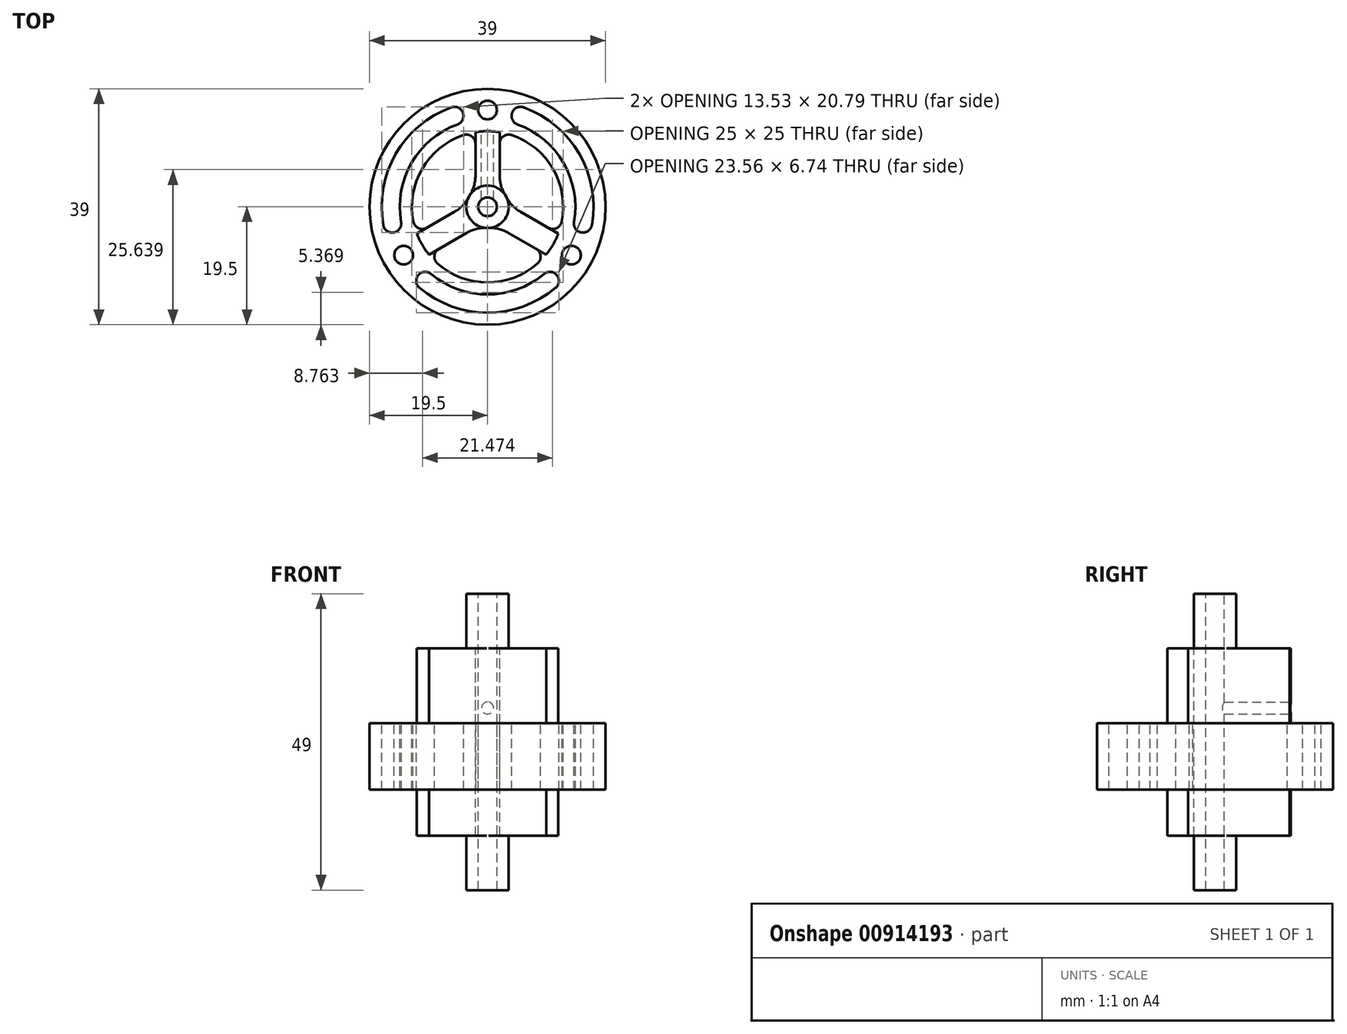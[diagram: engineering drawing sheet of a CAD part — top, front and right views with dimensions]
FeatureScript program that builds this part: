
annotation { "Feature Type Name" : "Feature", "Feature Type Description" : "" }
export const myFeature = defineFeature(function(context is Context, id is Id, definition is map)
    precondition{}
    {
        {
            var Q0;
            Q0=qCreatedBy(makeId("Front.planeOp"),FACE);
            var sketch = newSketch(context, id + "F0", { "sketchPlane" : qUnion([Q0])});
            skLineSegment(sketch, "E0", {"start": v(1.55, 49) * mm, "end": v(3.5, 49) * mm});
            skLineSegment(sketch, "E1", {"start": v(3.5, 49) * mm, "end": v(3.5, 40) * mm});
            skLineSegment(sketch, "E2", {"start": v(3.5, 40) * mm, "end": v(12.5, 40) * mm});
            skLineSegment(sketch, "E3", {"start": v(12.5, 40) * mm, "end": v(12.5, 27.6) * mm});
            skLineSegment(sketch, "E4", {"start": v(12.5, 27.6) * mm, "end": v(19.5, 27.6) * mm});
            skLineSegment(sketch, "E5", {"start": v(19.5, 27.6) * mm, "end": v(19.5, 16.6) * mm});
            skLineSegment(sketch, "E6", {"start": v(19.5, 16.6) * mm, "end": v(12.5, 16.6) * mm});
            skLineSegment(sketch, "E7", {"start": v(12.5, 16.6) * mm, "end": v(12.5, 9) * mm});
            skLineSegment(sketch, "E8", {"start": v(12.5, 9) * mm, "end": v(3.5, 9) * mm});
            skLineSegment(sketch, "E9", {"start": v(3.5, 9) * mm, "end": v(3.5, 0) * mm});
            skLineSegment(sketch, "E10", {"start": v(3.5, 0) * mm, "end": v(1.55, 0) * mm});
            skLineSegment(sketch, "E11", {"start": v(1.55, 49) * mm, "end": v(1.55, 0) * mm});
            skLineSegment(sketch, "E12", {"start": v(0, 52.95) * mm, "end": v(0, -2.67) * mm, "construction": true});
            skSolve(sketch);
        }
        {
            var Q0;
            Q0=makeQuery(id+"F0.imprint","IMPRINT",FACE,{"disambiguationData":[TD([[makeQuery(id+"F0.imprint","IMPRINT",EDGE,{"derivedFrom":sQuery(id+"F0.wireOp",EDGE,"E0")}),-1.0]])]});
            var Q1;
            Q1=sQuery(id+"F0.wireOp",EDGE,"E12");
            revolve(context, id + "F1", {"surfaceOperationType" : NewSurfaceOperationType.NEW, "entities" : qUnion([Q0]), "axis" : qUnion([Q1]), "revolveType" : RevolveType.FULL});
        }
        {
            var Q0;
            Q0=makeQuery(id+"F1.opRevolve","SWEPT_FACE",FACE,{"disambiguationData":[OSD([sQuery(id+"F0.wireOp",EDGE,"E4")])]});
            var sketch = newSketch(context, id + "F2", { "sketchPlane" : qUnion([Q0])});
            skCircle(sketch, "E13", {"center": v(0, 16) * mm, "radius": 1.55 * mm});
            skCircle(sketch, "E14.1.0", {"center": v(-13.86, -8) * mm, "radius": 1.55 * mm});
            skCircle(sketch, "E14.2.0", {"center": v(13.86, -8) * mm, "radius": 1.55 * mm});
            skPoint(sketch, "E14.center", {"position": v(0, 0) * mm});
            skArc(sketch, "E15", {"start": v(5.99, 16.44) * mm, "mid": v(15.16, 8.75) * mm, "end": v(17.23, -3.04) * mm});
            skArc(sketch, "E16", {"start": v(4.96, 13.63) * mm, "mid": v(12.56, 7.25) * mm, "end": v(14.28, -2.52) * mm});
            skArc(sketch, "E17", {"start": v(14.28, -2.52) * mm, "mid": v(15.5, -4.26) * mm, "end": v(17.23, -3.04) * mm});
            skArc(sketch, "E18", {"start": v(4.96, 13.63) * mm, "mid": v(4.06, 15.55) * mm, "end": v(5.99, 16.44) * mm});
            skLineSegment(sketch, "E19", {"start": v(0, 0) * mm, "end": v(5.47, 15.04) * mm, "construction": true});
            skLineSegment(sketch, "E20", {"start": v(0, 0) * mm, "end": v(15.76, -2.78) * mm, "construction": true});
            skArc(sketch, "E21.1.0", {"start": v(-14.28, -2.52) * mm, "mid": v(-12.56, 7.25) * mm, "end": v(-4.96, 13.63) * mm});
            skArc(sketch, "E21.1.1", {"start": v(-14.28, -2.52) * mm, "mid": v(-15.5, -4.26) * mm, "end": v(-17.23, -3.04) * mm});
            skArc(sketch, "E21.1.2", {"start": v(-17.23, -3.04) * mm, "mid": v(-15.16, 8.75) * mm, "end": v(-5.99, 16.44) * mm});
            skArc(sketch, "E21.1.3", {"start": v(-4.96, 13.63) * mm, "mid": v(-4.06, 15.55) * mm, "end": v(-5.99, 16.44) * mm});
            skArc(sketch, "E21.2.0", {"start": v(9.32, -11.1) * mm, "mid": v(0, -14.5) * mm, "end": v(-9.32, -11.1) * mm});
            skArc(sketch, "E21.2.1", {"start": v(9.32, -11.1) * mm, "mid": v(11.43, -11.3) * mm, "end": v(11.25, -13.4) * mm});
            skArc(sketch, "E21.2.2", {"start": v(11.25, -13.4) * mm, "mid": v(0, -17.5) * mm, "end": v(-11.25, -13.4) * mm});
            skArc(sketch, "E21.2.3", {"start": v(-9.32, -11.1) * mm, "mid": v(-11.43, -11.3) * mm, "end": v(-11.25, -13.4) * mm});
            skSolve(sketch);
        }
        {
            var Q0;
            Q0 = qSketchRegion(id + "F2", true);
            extrude(context, id + "F3", {"entities" : qUnion([Q0]), "operationType" : NewBodyOperationType.REMOVE, "endBound" : BoundingType.THROUGH_ALL, "oppositeDirection" : true, "depth" : 25 * mm, "offsetDistance" : 25 * mm});
        }
        {
            var Q0;
            Q0=makeQuery(id+"F1.opRevolve","SWEPT_FACE",FACE,{"disambiguationData":[OSD([sQuery(id+"F0.wireOp",EDGE,"E2")])]});
            var sketch = newSketch(context, id + "F4", { "sketchPlane" : qUnion([Q0])});
            skLineSegment(sketch, "E22", {"start": v(2, 5.12) * mm, "end": v(2, 12.34) * mm});
            skLineSegment(sketch, "E23", {"start": v(0, 0) * mm, "end": v(18.8, -10.86) * mm, "construction": true});
            skLineSegment(sketch, "E24", {"start": v(5.44, -0.83) * mm, "end": v(11.69, -4.44) * mm});
            skArc(sketch, "E25", {"start": v(2, 12.34) * mm, "mid": v(10.83, 6.25) * mm, "end": v(11.69, -4.44) * mm});
            skArc(sketch, "E26", {"start": v(2.95, 1.89) * mm, "mid": v(3.03, 1.75) * mm, "end": v(3.1, 1.6) * mm});
            skPoint(sketch, "E27.visualSharp", {"position": v(2, 12.34) * mm});
            skPoint(sketch, "E28.visualSharp", {"position": v(11.69, -4.44) * mm});
            skLineSegment(sketch, "E29.1.0", {"start": v(-5.44, -0.83) * mm, "end": v(-11.69, -4.44) * mm});
            skArc(sketch, "E29.1.1", {"start": v(-11.69, -4.44) * mm, "mid": v(-10.83, 6.25) * mm, "end": v(-2, 12.34) * mm});
            skLineSegment(sketch, "E29.1.2", {"start": v(-2, 5.12) * mm, "end": v(-2, 12.34) * mm});
            skArc(sketch, "E29.1.3", {"start": v(-3.1, 1.6) * mm, "mid": v(-3.03, 1.75) * mm, "end": v(-2.95, 1.89) * mm});
            skLineSegment(sketch, "E29.2.0", {"start": v(3.44, -4.3) * mm, "end": v(9.69, -7.9) * mm});
            skArc(sketch, "E29.2.1", {"start": v(9.69, -7.9) * mm, "mid": v(0, -12.5) * mm, "end": v(-9.69, -7.9) * mm});
            skLineSegment(sketch, "E29.2.2", {"start": v(-3.44, -4.3) * mm, "end": v(-9.69, -7.9) * mm});
            skArc(sketch, "E29.2.3", {"start": v(0.16, -3.5) * mm, "mid": v(0, -3.5) * mm, "end": v(-0.16, -3.5) * mm});
            skPoint(sketch, "E30.visualSharp", {"position": v(2, 2.87) * mm});
            skArc(sketch, "E30.filletArc", {"start": v(2, 5.12) * mm, "mid": v(2.24, 3.44) * mm, "end": v(2.95, 1.89) * mm});
            skPoint(sketch, "E31.visualSharp", {"position": v(3.49, 0.3) * mm});
            skArc(sketch, "E31.filletArc", {"start": v(3.1, 1.6) * mm, "mid": v(4.1, 0.22) * mm, "end": v(5.44, -0.83) * mm});
            skPoint(sketch, "E32.visualSharp", {"position": v(1.49, -3.17) * mm});
            skArc(sketch, "E32.filletArc", {"start": v(3.44, -4.3) * mm, "mid": v(1.86, -3.66) * mm, "end": v(0.16, -3.5) * mm});
            skPoint(sketch, "E33.visualSharp", {"position": v(-1.49, -3.17) * mm});
            skArc(sketch, "E33.filletArc", {"start": v(-0.16, -3.5) * mm, "mid": v(-1.86, -3.66) * mm, "end": v(-3.44, -4.3) * mm});
            skPoint(sketch, "E34.visualSharp", {"position": v(-3.49, 0.3) * mm});
            skArc(sketch, "E34.filletArc", {"start": v(-5.44, -0.83) * mm, "mid": v(-4.1, 0.22) * mm, "end": v(-3.1, 1.6) * mm});
            skPoint(sketch, "E35.visualSharp", {"position": v(-2, 2.87) * mm});
            skArc(sketch, "E35.filletArc", {"start": v(-2.95, 1.89) * mm, "mid": v(-2.24, 3.44) * mm, "end": v(-2, 5.12) * mm});
            skSolve(sketch);
        }
        {
            var Q0;
            Q0 = qSketchRegion(id + "F4", true);
            extrude(context, id + "F5", {"entities" : qUnion([Q0]), "operationType" : NewBodyOperationType.REMOVE, "endBound" : BoundingType.THROUGH_ALL, "oppositeDirection" : true, "depth" : 25 * mm, "offsetDistance" : 25 * mm});
        }
        {
            var Q0;
            {var subQ0=sQuery(id+"F4.wireOp",EDGE,"E29.1.0");var subQ1=sQuery(id+"F4.wireOp",EDGE,"E29.1.1");Q0=makeQuery(id+"F5.boolean.opBoolean","COPY",EDGE,{"disambiguationData":[topologyDisambiguationEdgeConnected([makeQuery(id+"F5.opExtrude","SWEPT_FACE",FACE,{"disambiguationData":[OSD([subQ1])]})])],"derivedFrom":makeQuery(id+"F5.opExtrude","SWEPT_EDGE",EDGE,{"disambiguationData":[OSD([sQuery(id+"F0.wireOp",EDGE,"E2"),sQuery(id+"F0.wireOp",EDGE,"E3"),subQ0,subQ1])]})});}
            var Q1;
            {var subQ0=sQuery(id+"F4.wireOp",EDGE,"E29.2.1");var subQ1=sQuery(id+"F4.wireOp",EDGE,"E29.2.2");Q1=makeQuery(id+"F5.boolean.opBoolean","COPY",EDGE,{"disambiguationData":[topologyDisambiguationEdgeConnected([makeQuery(id+"F5.opExtrude","SWEPT_FACE",FACE,{"disambiguationData":[OSD([subQ0])]})])],"derivedFrom":makeQuery(id+"F5.opExtrude","SWEPT_EDGE",EDGE,{"disambiguationData":[OSD([sQuery(id+"F0.wireOp",EDGE,"E2"),sQuery(id+"F0.wireOp",EDGE,"E3"),subQ0,subQ1])]})});}
            var Q2;
            {var subQ0=sQuery(id+"F4.wireOp",EDGE,"E29.2.0");var subQ1=sQuery(id+"F4.wireOp",EDGE,"E29.2.1");Q2=makeQuery(id+"F5.boolean.opBoolean","COPY",EDGE,{"disambiguationData":[topologyDisambiguationEdgeConnected([makeQuery(id+"F5.opExtrude","SWEPT_FACE",FACE,{"disambiguationData":[OSD([subQ1])]})])],"derivedFrom":makeQuery(id+"F5.opExtrude","SWEPT_EDGE",EDGE,{"disambiguationData":[OSD([sQuery(id+"F0.wireOp",EDGE,"E2"),sQuery(id+"F0.wireOp",EDGE,"E3"),subQ0,subQ1])]})});}
            var Q3;
            {var subQ0=sQuery(id+"F4.wireOp",EDGE,"E24");var subQ1=sQuery(id+"F4.wireOp",EDGE,"E25");Q3=makeQuery(id+"F5.boolean.opBoolean","COPY",EDGE,{"disambiguationData":[topologyDisambiguationEdgeConnected([makeQuery(id+"F5.opExtrude","SWEPT_FACE",FACE,{"disambiguationData":[OSD([subQ1])]})])],"derivedFrom":makeQuery(id+"F5.opExtrude","SWEPT_EDGE",EDGE,{"disambiguationData":[OSD([sQuery(id+"F0.wireOp",EDGE,"E2"),sQuery(id+"F0.wireOp",EDGE,"E3"),subQ0,subQ1])]})});}
            var Q4;
            {var subQ0=sQuery(id+"F4.wireOp",EDGE,"E22");var subQ1=sQuery(id+"F4.wireOp",EDGE,"E25");Q4=makeQuery(id+"F5.boolean.opBoolean","COPY",EDGE,{"disambiguationData":[topologyDisambiguationEdgeConnected([makeQuery(id+"F5.opExtrude","SWEPT_FACE",FACE,{"disambiguationData":[OSD([subQ1])]})])],"derivedFrom":makeQuery(id+"F5.opExtrude","SWEPT_EDGE",EDGE,{"disambiguationData":[OSD([sQuery(id+"F0.wireOp",EDGE,"E2"),sQuery(id+"F0.wireOp",EDGE,"E3"),subQ0,subQ1])]})});}
            var Q5;
            {var subQ0=sQuery(id+"F4.wireOp",EDGE,"E29.1.1");var subQ1=sQuery(id+"F4.wireOp",EDGE,"E29.1.2");Q5=makeQuery(id+"F5.boolean.opBoolean","COPY",EDGE,{"disambiguationData":[topologyDisambiguationEdgeConnected([makeQuery(id+"F5.opExtrude","SWEPT_FACE",FACE,{"disambiguationData":[OSD([subQ0])]})])],"derivedFrom":makeQuery(id+"F5.opExtrude","SWEPT_EDGE",EDGE,{"disambiguationData":[OSD([sQuery(id+"F0.wireOp",EDGE,"E2"),sQuery(id+"F0.wireOp",EDGE,"E3"),subQ0,subQ1])]})});}
            fillet(context, id + "F6", {"entities" : qUnion([Q0, Q1, Q2, Q3, Q4, Q5]), "radius" : 1.5 * mm, "tangentPropagation" : true, "allowEdgeOverflow" : false});
        }
        {
            var Q0;
            Q0=qCreatedBy(makeId("Front.planeOp"),FACE);
            cPlane(context, id + "F7", {"entities" : qUnion([Q0]), "cplaneType" : CPlaneType.OFFSET, "offset" : 12.5 * mm, "oppositeDirection" : true, "width" : 150 * mm, "height" : 150 * mm});
        }
        {
            var Q0;
            Q0=qCreatedBy(id+"F7.planeOp",FACE);
            var sketch = newSketch(context, id + "F8", { "sketchPlane" : qUnion([Q0])});
            skCircle(sketch, "E36", {"center": v(0, 30.1) * mm, "radius": 1 * mm});
            skSolve(sketch);
        }
        {
            var Q0;
            Q0 = qSketchRegion(id + "F8", true);
            var Q1;
            Q1=qCreatedBy(makeId("Front.planeOp"),FACE);
            extrude(context, id + "F9", {"entities" : qUnion([Q0]), "operationType" : NewBodyOperationType.REMOVE, "endBound" : BoundingType.UP_TO_SURFACE, "depth" : 11.37 * mm, "endBoundEntityFace" : qUnion([Q1]), "offsetDistance" : 25 * mm});
        }
    });
